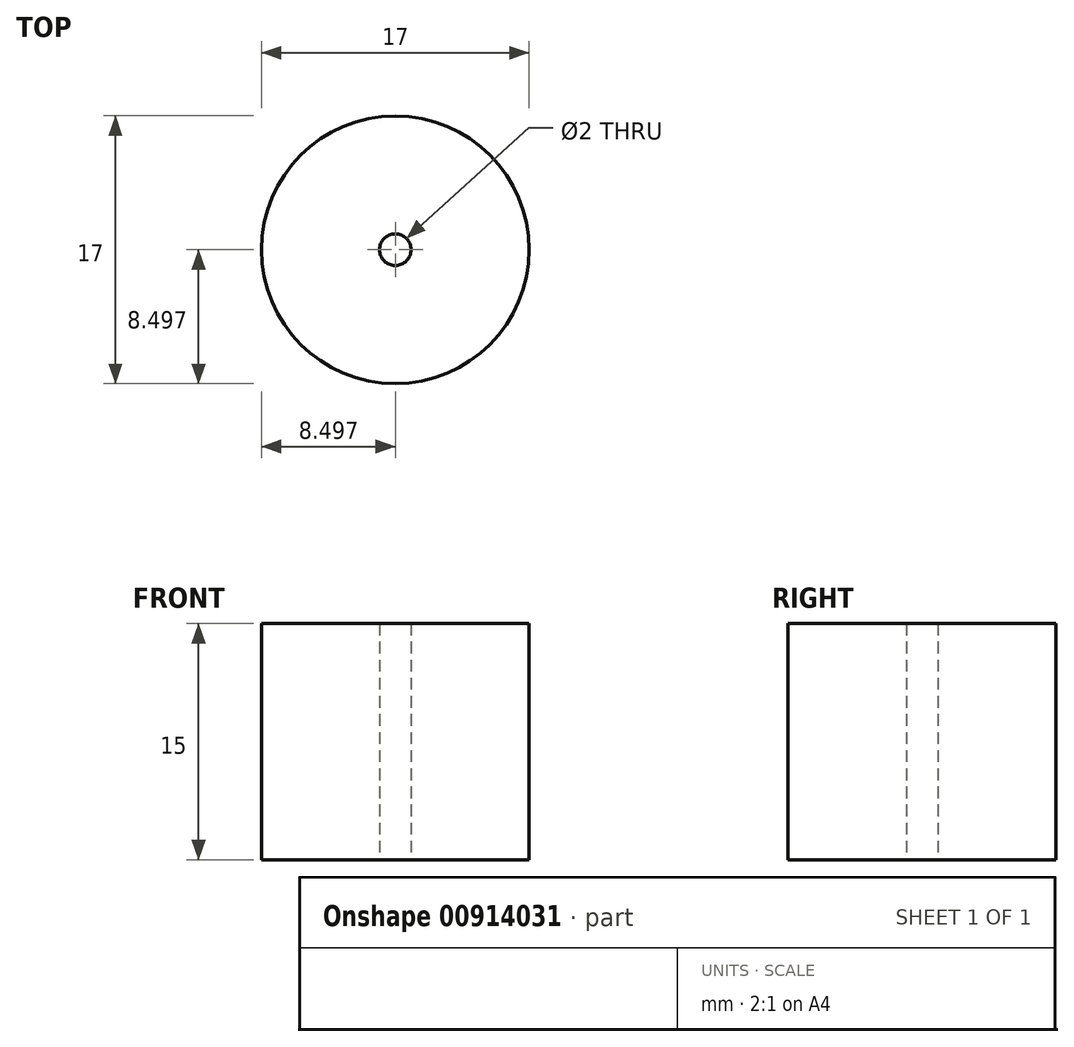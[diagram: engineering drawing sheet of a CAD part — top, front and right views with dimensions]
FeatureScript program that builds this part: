
annotation { "Feature Type Name" : "Feature", "Feature Type Description" : "" }
export const myFeature = defineFeature(function(context is Context, id is Id, definition is map)
    precondition{}
    {
        {
            var Q0;
            Q0=qCreatedBy(makeId("Top.planeOp"),FACE);
            var sketch = newSketch(context, id + "F0", { "sketchPlane" : qUnion([Q0])});
            skCircle(sketch, "E0", {"center": v(-41.78, 4.1) * mm, "radius": 1 * mm});
            skCircle(sketch, "E1", {"center": v(-41.78, 4.1) * mm, "radius": 8.5 * mm});
            skSolve(sketch);
        }
        {
            var Q0;
            Q0=makeQuery(id+"F0.imprint","IMPRINT",FACE,{"disambiguationData":[TD([[makeQuery(id+"F0.imprint","IMPRINT",EDGE,{"derivedFrom":sQuery(id+"F0.wireOp",EDGE,"E0")}),-1.0]])]});
            extrude(context, id + "F1", {"entities" : qUnion([Q0]), "depth" : 15 * mm, "offsetDistance" : 25 * mm});
        }
    });
